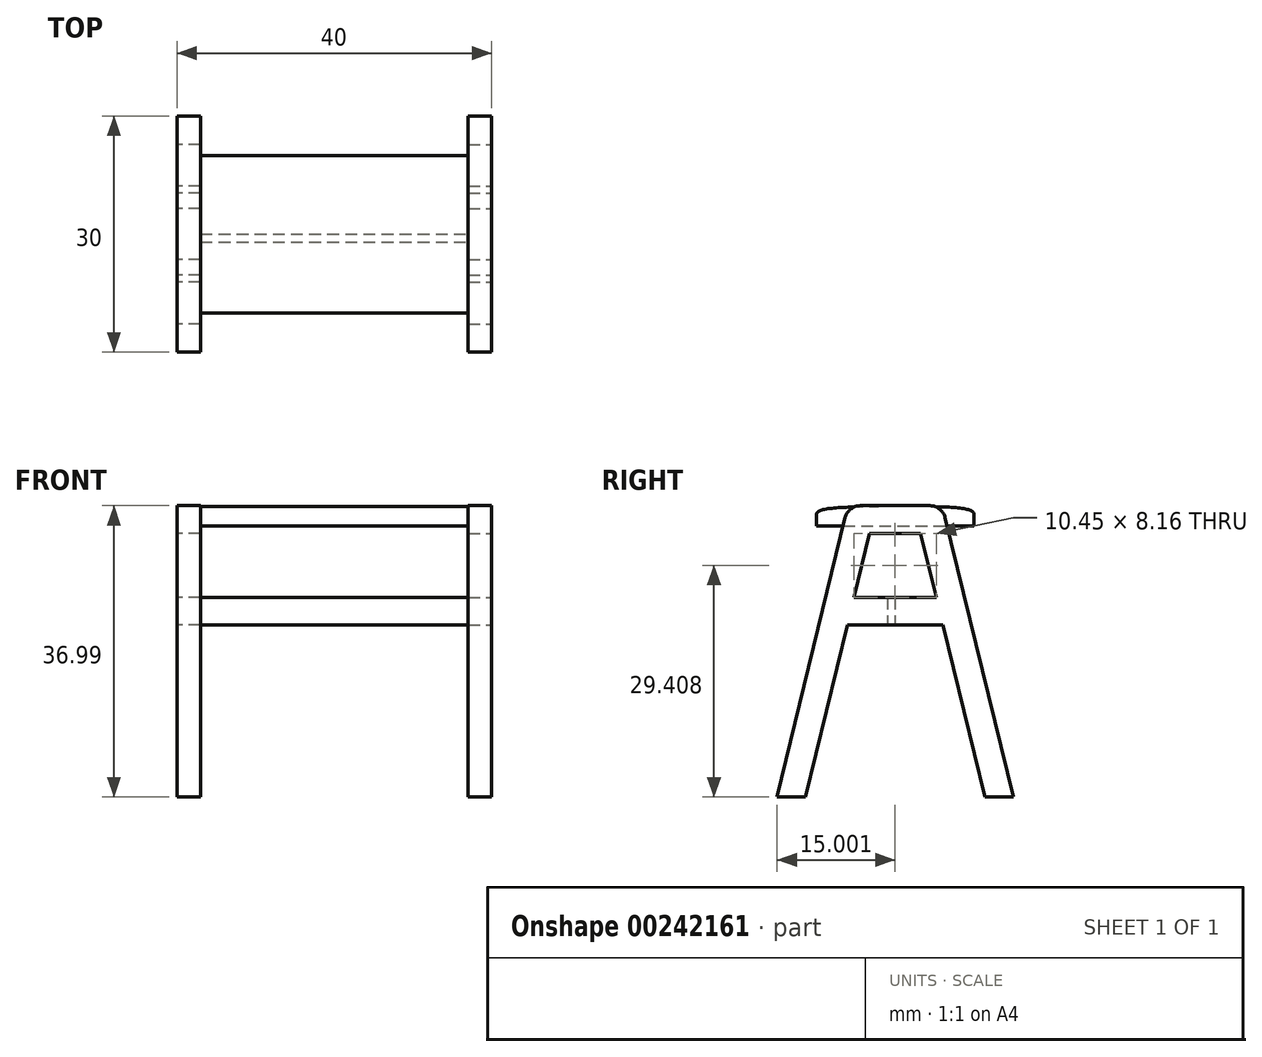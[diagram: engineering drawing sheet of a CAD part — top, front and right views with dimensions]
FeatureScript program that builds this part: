
annotation { "Feature Type Name" : "Feature", "Feature Type Description" : "" }
export const myFeature = defineFeature(function(context is Context, id is Id, definition is map)
    precondition{}
    {
        {
            var Q0;
            Q0=qCreatedBy(makeId("Right.planeOp"),FACE);
            var sketch = newSketch(context, id + "F0", { "sketchPlane" : qUnion([Q0])});
            skLineSegment(sketch, "E0.bottom", {"start": v(-193.89, 0) * mm, "end": v(-163.89, 0) * mm});
            skLineSegment(sketch, "E0.top", {"start": v(-193.89, 42) * mm, "end": v(-163.89, 42) * mm});
            skLineSegment(sketch, "E0.left", {"start": v(-193.89, 0) * mm, "end": v(-193.89, 42) * mm});
            skLineSegment(sketch, "E0.right", {"start": v(-163.89, 0) * mm, "end": v(-163.89, 42) * mm});
            skLineSegment(sketch, "E1", {"start": v(-178.89, 42) * mm, "end": v(-178.89, 0) * mm, "construction": true});
            skLineSegment(sketch, "E2", {"start": v(-163.89, 0) * mm, "end": v(-172.9, 36.99) * mm});
            skLineSegment(sketch, "E3", {"start": v(-172.9, 36.99) * mm, "end": v(-178.89, 36.99) * mm});
            skLineSegment(sketch, "E4.0", {"start": v(-175.65, 33.49) * mm, "end": v(-178.89, 33.49) * mm});
            skLineSegment(sketch, "E4.1", {"start": v(-167.5, 0) * mm, "end": v(-175.65, 33.49) * mm});
            skLineSegment(sketch, "E5", {"start": v(-173.67, 25.33) * mm, "end": v(-178.89, 25.33) * mm});
            skLineSegment(sketch, "E6", {"start": v(-178.89, 25.33) * mm, "end": v(-178.89, 21.83) * mm});
            skLineSegment(sketch, "E7", {"start": v(-178.89, 21.83) * mm, "end": v(-172.81, 21.83) * mm});
            skLineSegment(sketch, "E8.MirrorCS", {"start": v(-184.11, 25.33) * mm, "end": v(-178.89, 25.33) * mm});
            skLineSegment(sketch, "E9.MirrorCS", {"start": v(-178.89, 21.83) * mm, "end": v(-184.97, 21.83) * mm});
            skLineSegment(sketch, "E10.MirrorCS", {"start": v(-182.12, 33.49) * mm, "end": v(-178.89, 33.49) * mm});
            skLineSegment(sketch, "E11.MirrorCS", {"start": v(-190.29, 0) * mm, "end": v(-182.12, 33.49) * mm});
            skLineSegment(sketch, "E12.MirrorCS", {"start": v(-184.87, 36.99) * mm, "end": v(-178.89, 36.99) * mm});
            skLineSegment(sketch, "E13.MirrorCS", {"start": v(-193.89, 0) * mm, "end": v(-184.87, 36.99) * mm});
            skLineSegment(sketch, "E14", {"start": v(-163.89, 0) * mm, "end": v(-167.5, 0) * mm});
            skLineSegment(sketch, "E15", {"start": v(-190.29, 0) * mm, "end": v(-193.89, 0) * mm});
            skLineSegment(sketch, "E16.top", {"start": v(-169.58, 34.43) * mm, "end": v(-178.89, 34.43) * mm});
            skLineSegment(sketch, "E16.left", {"start": v(-169.58, 36.99) * mm, "end": v(-169.58, 34.43) * mm});
            skLineSegment(sketch, "E16.right", {"start": v(-178.89, 36.96) * mm, "end": v(-178.89, 34.43) * mm});
            skLineSegment(sketch, "E17.MirrorCS", {"start": v(-188.2, 34.43) * mm, "end": v(-178.89, 34.43) * mm});
            skLineSegment(sketch, "E18.MirrorCS", {"start": v(-188.2, 36.99) * mm, "end": v(-188.2, 34.43) * mm});
            skFitSpline(sketch, "E19", {"points": [v(-169.58, 36.99) * mm, v(-178.89, 38.9) * mm, v(-188.2, 36.99) * mm], "startDerivative": vector(-18.83, 9.2) * mm, "endDerivative": vector(-18.83, -9.2) * mm});
            skLineSegment(sketch, "E20.bottom", {"start": v(-178.89, 25.33) * mm, "end": v(-177.89, 25.33) * mm});
            skLineSegment(sketch, "E20.top", {"start": v(-178.89, 21.83) * mm, "end": v(-177.89, 21.83) * mm});
            skLineSegment(sketch, "E20.right", {"start": v(-177.89, 25.33) * mm, "end": v(-177.89, 21.83) * mm});
            skLineSegment(sketch, "E21.MirrorCS", {"start": v(-179.89, 25.33) * mm, "end": v(-179.89, 21.83) * mm});
            skSolve(sketch);
        }
        {
            var Q0;
            {var subQ6=sQuery(id+"F0.wireOp",EDGE,"E4.0");Q0=makeQuery(id+"F0.imprint","IMPRINT",FACE,{"disambiguationData":[TD([[makeQuery(id+"F0.imprint","IMPRINT",EDGE,{"derivedFrom":subQ6}),-1.0]])]});}
            var Q1;
            {var subQ4=sQuery(id+"F0.wireOp",EDGE,"E3");Q1=makeQuery(id+"F0.imprint","IMPRINT",FACE,{"disambiguationData":[TD([[makeQuery(id+"F0.imprint","IMPRINT",EDGE,{"derivedFrom":subQ4}),1.0]])]});}
            var Q2;
            {var subQ3=sQuery(id+"F0.wireOp",EDGE,"E21.MirrorCS");Q2=makeQuery(id+"F0.imprint","IMPRINT",FACE,{"disambiguationData":[TD([[makeQuery(id+"F0.imprint","IMPRINT",EDGE,{"derivedFrom":subQ3}),-1.0]])]});}
            var Q3;
            Q3=makeQuery(id+"F0.imprint","IMPRINT",FACE,{"disambiguationData":[TD([[makeQuery(id+"F0.imprint","IMPRINT",EDGE,{"derivedFrom":sQuery(id+"F0.wireOp",EDGE,"E20.bottom")}),-1.0]])]});
            var Q4;
            {var subQ0=sQuery(id+"F0.wireOp",EDGE,"E6");Q4=makeQuery(id+"F0.imprint","IMPRINT",FACE,{"disambiguationData":[TD([[makeQuery(id+"F0.imprint","IMPRINT",EDGE,{"derivedFrom":subQ0}),-1.0]])]});}
            var Q5;
            {var subQ0=sQuery(id+"F0.wireOp",EDGE,"E5");Q5=makeQuery(id+"F0.imprint","IMPRINT",FACE,{"disambiguationData":[TD([[makeQuery(id+"F0.imprint","IMPRINT",EDGE,{"derivedFrom":subQ0}),1.0]])]});}
            extrude(context, id + "F1", {"entities" : qUnion([Q0, Q1, Q2, Q3, Q4, Q5]), "oppositeDirection" : true, "depth" : 3 * mm});
        }
        {
            var Q0;
            {var subQ0=sQuery(id+"F0.wireOp",EDGE,"E6");Q0=makeQuery(id+"F0.imprint","IMPRINT",FACE,{"disambiguationData":[TD([[makeQuery(id+"F0.imprint","IMPRINT",EDGE,{"derivedFrom":subQ0}),-1.0]])]});}
            var Q1;
            Q1=makeQuery(id+"F0.imprint","IMPRINT",FACE,{"disambiguationData":[TD([[makeQuery(id+"F0.imprint","IMPRINT",EDGE,{"derivedFrom":sQuery(id+"F0.wireOp",EDGE,"E20.bottom")}),-1.0]])]});
            extrude(context, id + "F2", {"entities" : qUnion([Q0, Q1]), "operationType" : NewBodyOperationType.ADD, "oppositeDirection" : true, "depth" : 20 * mm});
        }
        {
            var Q0;
            Q0=makeQuery(id+"F1.opExtrude","CAP_FACE",FACE,{"disambiguationData":[OSD([sQuery(id+"F0.wireOp",EDGE,"E2"),sQuery(id+"F0.wireOp",EDGE,"E3"),sQuery(id+"F0.wireOp",EDGE,"E4.0"),sQuery(id+"F0.wireOp",EDGE,"E4.1"),sQuery(id+"F0.wireOp",EDGE,"E5"),sQuery(id+"F0.wireOp",EDGE,"E7"),sQuery(id+"F0.wireOp",EDGE,"E8.MirrorCS"),sQuery(id+"F0.wireOp",EDGE,"E9.MirrorCS"),sQuery(id+"F0.wireOp",EDGE,"E10.MirrorCS"),sQuery(id+"F0.wireOp",EDGE,"E11.MirrorCS"),sQuery(id+"F0.wireOp",EDGE,"E12.MirrorCS"),sQuery(id+"F0.wireOp",EDGE,"E13.MirrorCS"),sQuery(id+"F0.wireOp",EDGE,"E14"),sQuery(id+"F0.wireOp",EDGE,"E15"),sQuery(id+"F0.wireOp",EDGE,"E20.bottom"),sQuery(id+"F0.wireOp",EDGE,"E20.top")])],"isStart":false});
            var sketch = newSketch(context, id + "F3", { "sketchPlane" : qUnion([Q0])});
            skLineSegment(sketch, "E22.top", {"start": v(178.89, 34.43) * mm, "end": v(168.89, 34.43) * mm});
            skLineSegment(sketch, "E22.left", {"start": v(168.89, 35.93) * mm, "end": v(168.89, 34.43) * mm});
            skFitSpline(sketch, "E23", {"points": [v(168.89, 35.93) * mm, v(178.89, 36.86) * mm, v(188.89, 35.93) * mm], "startDerivative": vector(0, 6.35) * mm, "endDerivative": vector(0, -5.92) * mm});
            skLineSegment(sketch, "E24", {"start": v(178.89, 33.49) * mm, "end": v(178.89, 40.24) * mm, "construction": true});
            skPoint(sketch, "E25", {"position": v(178.89, 36.99) * mm});
            skLineSegment(sketch, "E26.MirrorCS", {"start": v(178.89, 34.43) * mm, "end": v(188.89, 34.43) * mm});
            skLineSegment(sketch, "E27.MirrorCS", {"start": v(188.89, 35.93) * mm, "end": v(188.89, 34.43) * mm});
            skSolve(sketch);
        }
        {
            var Q0;
            {var subQ0=sQuery(id+"F3.wireOp",EDGE,"E22.left");Q0=makeQuery(id+"F3.imprint","IMPRINT",FACE,{"disambiguationData":[TD([[makeQuery(id+"F3.imprint","IMPRINT",EDGE,{"derivedFrom":subQ0}),1.0]])]});}
            var Q1;
            {var subQ0=sQuery(id+"F3.wireOp",EDGE,"E27.MirrorCS");Q1=makeQuery(id+"F3.imprint","IMPRINT",FACE,{"disambiguationData":[TD([[makeQuery(id+"F3.imprint","IMPRINT",EDGE,{"derivedFrom":subQ0}),-1.0]])]});}
            var Q2;
            {var subQ0=sQuery(id+"F3.wireOp",EDGE,"E22.top");var subQ5=sQuery(id+"F3.wireOp",EDGE,"E26.MirrorCS");var subQ6=makeQuery(id+"F3.imprint","INTERSECT",VERTEX,{"derivedFrom":[subQ0,subQ5]});Q2=makeQuery(id+"F3.imprint","IMPRINT",FACE,{"disambiguationData":[TD([[makeQuery(id+"F3.imprint","IMPRINT",EDGE,{"disambiguationData":[TD([[subQ6,-1.0]])],"derivedFrom":subQ0}),-1.0]])]});}
            var Q3;
            Q3=makeQuery(id+"F2.opExtrude","CAP_FACE",FACE,{"disambiguationData":[OSD([sQuery(id+"F0.wireOp",EDGE,"E8.MirrorCS"),sQuery(id+"F0.wireOp",EDGE,"E9.MirrorCS"),sQuery(id+"F0.wireOp",EDGE,"E20.bottom"),sQuery(id+"F0.wireOp",EDGE,"E20.top"),sQuery(id+"F0.wireOp",EDGE,"E20.right"),sQuery(id+"F0.wireOp",EDGE,"E21.MirrorCS")])],"isStart":false});
            extrude(context, id + "F4", {"entities" : qUnion([Q0, Q1, Q2]), "operationType" : NewBodyOperationType.ADD, "endBound" : BoundingType.UP_TO_SURFACE, "endBoundEntityFace" : qUnion([Q3]), "depth" : 25 * mm});
        }
        {
            var Q0;
            Q0=makeQuery(id+"F1.opExtrude","SWEPT_BODY",BODY,{"disambiguationData":[OSD([sQuery(id+"F0.wireOp",EDGE,"E2"),sQuery(id+"F0.wireOp",EDGE,"E3"),sQuery(id+"F0.wireOp",EDGE,"E4.0"),sQuery(id+"F0.wireOp",EDGE,"E4.1"),sQuery(id+"F0.wireOp",EDGE,"E5"),sQuery(id+"F0.wireOp",EDGE,"E7"),sQuery(id+"F0.wireOp",EDGE,"E8.MirrorCS"),sQuery(id+"F0.wireOp",EDGE,"E9.MirrorCS"),sQuery(id+"F0.wireOp",EDGE,"E10.MirrorCS"),sQuery(id+"F0.wireOp",EDGE,"E11.MirrorCS"),sQuery(id+"F0.wireOp",EDGE,"E12.MirrorCS"),sQuery(id+"F0.wireOp",EDGE,"E13.MirrorCS"),sQuery(id+"F0.wireOp",EDGE,"E14"),sQuery(id+"F0.wireOp",EDGE,"E15"),sQuery(id+"F0.wireOp",EDGE,"E20.bottom"),sQuery(id+"F0.wireOp",EDGE,"E20.top")])]});
            var Q1;
            Q1=makeQuery(id+"F4.opExtrude","CAP_FACE",FACE,{"disambiguationData":[OSD([sQuery(id+"F3.wireOp",EDGE,"E22.top"),sQuery(id+"F3.wireOp",EDGE,"E22.left"),sQuery(id+"F3.wireOp",EDGE,"E23"),sQuery(id+"F3.wireOp",EDGE,"E26.MirrorCS"),sQuery(id+"F3.wireOp",EDGE,"E27.MirrorCS")])],"isStart":false});
            mirror(context, id + "F5", {"operationType" : NewBodyOperationType.ADD, "entities" : qUnion([Q0]), "mirrorPlane" : qUnion([Q1])});
        }
        {
            var Q0;
            Q0=makeQuery(id+"F1.opExtrude","SWEPT_EDGE",EDGE,{"disambiguationData":[OSD([sQuery(id+"F0.wireOp",EDGE,"E12.MirrorCS"),sQuery(id+"F0.wireOp",EDGE,"E13.MirrorCS")])]});
            var Q1;
            Q1=makeQuery(id+"F5.opPattern","COPY",EDGE,{"derivedFrom":makeQuery(id+"F1.opExtrude","SWEPT_EDGE",EDGE,{"disambiguationData":[OSD([sQuery(id+"F0.wireOp",EDGE,"E12.MirrorCS"),sQuery(id+"F0.wireOp",EDGE,"E13.MirrorCS")])]}),"instanceName":"1"});
            var Q2;
            Q2=makeQuery(id+"F5.opPattern","COPY",EDGE,{"derivedFrom":makeQuery(id+"F1.opExtrude","SWEPT_EDGE",EDGE,{"disambiguationData":[OSD([sQuery(id+"F0.wireOp",EDGE,"E2"),sQuery(id+"F0.wireOp",EDGE,"E3")])]}),"instanceName":"1"});
            var Q3;
            Q3=makeQuery(id+"F1.opExtrude","SWEPT_EDGE",EDGE,{"disambiguationData":[OSD([sQuery(id+"F0.wireOp",EDGE,"E2"),sQuery(id+"F0.wireOp",EDGE,"E3")])]});
            fillet(context, id + "F6", {"entities" : qUnion([Q0, Q1, Q2, Q3]), "radius" : 2 * mm, "tangentPropagation" : true, "allowEdgeOverflow" : false});
        }
    });
